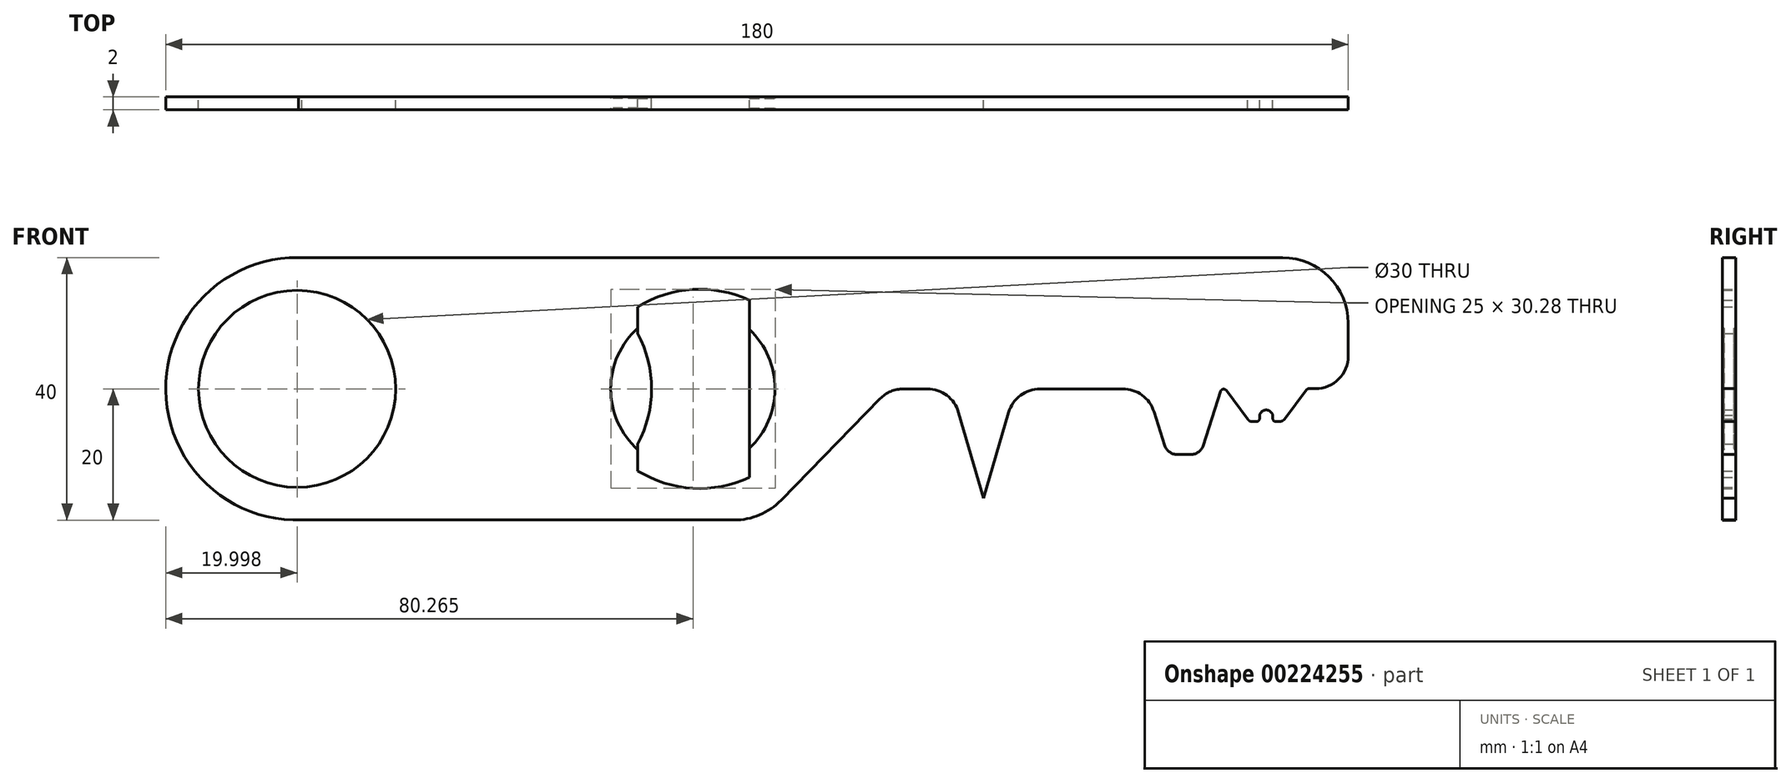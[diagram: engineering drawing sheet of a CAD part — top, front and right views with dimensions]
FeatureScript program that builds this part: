
annotation { "Feature Type Name" : "Feature", "Feature Type Description" : "" }
export const myFeature = defineFeature(function(context is Context, id is Id, definition is map)
    precondition{}
    {
        {
            var Q0;
            Q0=qCreatedBy(makeId("Front.planeOp"),FACE);
            var sketch = newSketch(context, id + "F0", { "sketchPlane" : qUnion([Q0])});
            skArc(sketch, "E0", {"start": v(-75.03, 20) * mm, "mid": v(-95.23, -0.26) * mm, "end": v(-74.5, -19.99) * mm});
            skLineSegment(sketch, "E1", {"start": v(-75.03, 20) * mm, "end": v(74.77, 20) * mm});
            skLineSegment(sketch, "E2", {"start": v(84.77, 10) * mm, "end": v(84.77, 5.03) * mm});
            skLineSegment(sketch, "E3", {"start": v(-74.5, -19.99) * mm, "end": v(-8.73, -19.99) * mm});
            skLineSegment(sketch, "E4", {"start": v(-1.56, -16.97) * mm, "end": v(13.5, -1.5) * mm});
            skCircle(sketch, "E5", {"center": v(-75.23, 0) * mm, "radius": 15 * mm});
            skPoint(sketch, "E6.start.orphan", {"position": v(-95.23, 0) * mm});
            skLineSegment(sketch, "E7", {"start": v(79.77, 0.03) * mm, "end": v(78.79, 0.03) * mm});
            skLineSegment(sketch, "E8", {"start": v(74.27, -5) * mm, "end": v(73.77, -5) * mm});
            skLineSegment(sketch, "E9", {"start": v(60.8, -10) * mm, "end": v(58.73, -10) * mm});
            skLineSegment(sketch, "E10.trimOffspring", {"start": v(70.77, -5) * mm, "end": v(70.1, -5) * mm});
            skArc(sketch, "E11", {"start": v(73.27, -4) * mm, "mid": v(72.27, -3.22) * mm, "end": v(71.27, -4) * mm});
            skLineSegment(sketch, "E12", {"start": v(73.27, -4.5) * mm, "end": v(73.27, -4) * mm});
            skLineSegment(sketch, "E13", {"start": v(71.27, -4.5) * mm, "end": v(71.27, -4) * mm});
            skArc(sketch, "E14.filletArc", {"start": v(73.27, -4.5) * mm, "mid": v(73.41, -4.85) * mm, "end": v(73.77, -5) * mm});
            skArc(sketch, "E15.filletArc", {"start": v(70.77, -5) * mm, "mid": v(71.12, -4.85) * mm, "end": v(71.27, -4.5) * mm});
            skLineSegment(sketch, "E16", {"start": v(75.07, -4.6) * mm, "end": v(78.39, -0.17) * mm});
            skArc(sketch, "E17.filletArc", {"start": v(74.27, -5) * mm, "mid": v(74.71, -4.9) * mm, "end": v(75.07, -4.6) * mm});
            skLineSegment(sketch, "E18", {"start": v(72.27, -20) * mm, "end": v(29.27, -20) * mm});
            skLineSegment(sketch, "E19", {"start": v(62.71, -8.6) * mm, "end": v(65.32, -0.39) * mm});
            skLineSegment(sketch, "E20.MirrorCS", {"start": v(69.47, -4.6) * mm, "end": v(66.2, -0.24) * mm});
            skArc(sketch, "E21", {"start": v(69.47, -4.6) * mm, "mid": v(69.73, -4.9) * mm, "end": v(70.1, -5) * mm});
            skPoint(sketch, "E22.endSnap0", {"position": v(59.77, -10) * mm});
            skLineSegment(sketch, "E23.MirrorCS", {"start": v(56.82, -8.6) * mm, "end": v(55.2, -3.49) * mm});
            skPoint(sketch, "E24.newPointA", {"position": v(65.45, 0) * mm});
            skArc(sketch, "E24.filletArc", {"start": v(66.2, -0.24) * mm, "mid": v(65.72, -0.05) * mm, "end": v(65.32, -0.39) * mm});
            skPoint(sketch, "E25.visualSharp", {"position": v(57.27, -10) * mm});
            skArc(sketch, "E25.filletArc", {"start": v(56.82, -8.6) * mm, "mid": v(57.55, -9.61) * mm, "end": v(58.73, -10) * mm});
            skPoint(sketch, "E26.visualSharp", {"position": v(62.27, -10) * mm});
            skArc(sketch, "E26.filletArc", {"start": v(60.8, -10) * mm, "mid": v(61.99, -9.61) * mm, "end": v(62.71, -8.6) * mm});
            skLineSegment(sketch, "E27", {"start": v(25.46, -3.6) * mm, "end": v(29.25, -16.67) * mm});
            skLineSegment(sketch, "E28", {"start": v(33.07, -3.6) * mm, "end": v(29.25, -16.67) * mm});
            skLineSegment(sketch, "E29", {"start": v(17.08, 0) * mm, "end": v(20.66, 0) * mm});
            skLineSegment(sketch, "E30", {"start": v(37.87, 0) * mm, "end": v(50.43, 0) * mm});
            skPoint(sketch, "E31.visualSharp", {"position": v(24.42, 0) * mm});
            skArc(sketch, "E31.filletArc", {"start": v(25.46, -3.6) * mm, "mid": v(23.66, -1) * mm, "end": v(20.66, 0) * mm});
            skPoint(sketch, "E32.visualSharp", {"position": v(14.97, 0) * mm});
            skArc(sketch, "E32.filletArc", {"start": v(17.08, 0) * mm, "mid": v(15.14, -0.4) * mm, "end": v(13.5, -1.5) * mm});
            skPoint(sketch, "E33.visualSharp", {"position": v(34.12, 0) * mm});
            skArc(sketch, "E33.filletArc", {"start": v(37.87, 0) * mm, "mid": v(34.87, -1) * mm, "end": v(33.07, -3.6) * mm});
            skPoint(sketch, "E34.visualSharp", {"position": v(54.1, 0) * mm});
            skArc(sketch, "E34.filletArc", {"start": v(55.2, -3.49) * mm, "mid": v(53.38, -0.96) * mm, "end": v(50.43, 0) * mm});
            skLineSegment(sketch, "E35", {"start": v(72.27, -16.33) * mm, "end": v(62.27, -16.33) * mm});
            skPoint(sketch, "E36.visualSharp", {"position": v(84.77, 20) * mm});
            skArc(sketch, "E36.filletArc", {"start": v(84.77, 10) * mm, "mid": v(81.84, 17.07) * mm, "end": v(74.77, 20) * mm});
            skPoint(sketch, "E37.visualSharp", {"position": v(84.77, 0.03) * mm});
            skArc(sketch, "E37.filletArc", {"start": v(79.77, 0.03) * mm, "mid": v(83.3, 1.5) * mm, "end": v(84.77, 5.03) * mm});
            skPoint(sketch, "E38.visualSharp", {"position": v(78.54, 0.03) * mm});
            skArc(sketch, "E38.filletArc", {"start": v(78.79, 0.03) * mm, "mid": v(78.56, -0.03) * mm, "end": v(78.39, -0.17) * mm});
            skPoint(sketch, "E39.visualSharp", {"position": v(-4.5, -19.99) * mm});
            skArc(sketch, "E39.filletArc", {"start": v(-8.73, -19.99) * mm, "mid": v(-4.84, -19.2) * mm, "end": v(-1.56, -16.97) * mm});
            skSolve(sketch);
        }
        {
            var Q0;
            Q0=makeQuery(id+"F0.imprint","IMPRINT",FACE,{"disambiguationData":[TD([[makeQuery(id+"F0.imprint","IMPRINT",EDGE,{"derivedFrom":sQuery(id+"F0.wireOp",EDGE,"E0")}),1.0]])]});
            extrude(context, id + "F1", {"entities" : qUnion([Q0]), "depth" : 2 * mm});
        }
        {
            var Q0;
            Q0=qCreatedBy(makeId("Front.planeOp"),FACE);
            var sketch = newSketch(context, id + "F2", { "sketchPlane" : qUnion([Q0])});
            skLineSegment(sketch, "E40", {"start": v(-6.37, 0) * mm, "end": v(-6.37, -13.5) * mm});
            skLineSegment(sketch, "E41", {"start": v(-6.37, 0) * mm, "end": v(-6.37, 13.5) * mm});
            skLineSegment(sketch, "E42", {"start": v(-23.37, 8.41) * mm, "end": v(-23.37, 12.5) * mm});
            skLineSegment(sketch, "E43", {"start": v(-23.37, -8.41) * mm, "end": v(-23.37, -12.5) * mm});
            skArc(sketch, "E44", {"start": v(-6.37, 13.5) * mm, "mid": v(-15, 15.14) * mm, "end": v(-23.37, 12.5) * mm});
            skArc(sketch, "E45", {"start": v(-23.37, -12.5) * mm, "mid": v(-15, -15.14) * mm, "end": v(-6.37, -13.5) * mm});
            skArc(sketch, "E46", {"start": v(-23.37, -8.41) * mm, "mid": v(-21.28, 0) * mm, "end": v(-23.37, 8.41) * mm});
            skPoint(sketch, "E47.orphan", {"position": v(-23.37, 0) * mm});
            skSolve(sketch);
        }
        {
            var Q0;
            Q0=makeQuery(id+"F2.imprint","IMPRINT",FACE,{"disambiguationData":[TD([[makeQuery(id+"F2.imprint","IMPRINT",EDGE,{"derivedFrom":sQuery(id+"F2.wireOp",EDGE,"E40")}),-1.0]])]});
            extrude(context, id + "F3", {"entities" : qUnion([Q0]), "operationType" : NewBodyOperationType.REMOVE, "endBound" : BoundingType.THROUGH_ALL, "depth" : 25 * mm});
        }
        {
            var Q0;
            Q0=makeQuery(id+"F1.opExtrude","CAP_FACE",FACE,{"disambiguationData":[OSD([sQuery(id+"F0.wireOp",EDGE,"E0"),sQuery(id+"F0.wireOp",EDGE,"E1"),sQuery(id+"F0.wireOp",EDGE,"E2"),sQuery(id+"F0.wireOp",EDGE,"E3"),sQuery(id+"F0.wireOp",EDGE,"E4"),sQuery(id+"F0.wireOp",EDGE,"E5"),sQuery(id+"F0.wireOp",EDGE,"E7"),sQuery(id+"F0.wireOp",EDGE,"E8"),sQuery(id+"F0.wireOp",EDGE,"E9"),sQuery(id+"F0.wireOp",EDGE,"E10.trimOffspring"),sQuery(id+"F0.wireOp",EDGE,"E11"),sQuery(id+"F0.wireOp",EDGE,"E12"),sQuery(id+"F0.wireOp",EDGE,"E13"),sQuery(id+"F0.wireOp",EDGE,"E14.filletArc"),sQuery(id+"F0.wireOp",EDGE,"E15.filletArc"),sQuery(id+"F0.wireOp",EDGE,"E16"),sQuery(id+"F0.wireOp",EDGE,"E17.filletArc"),sQuery(id+"F0.wireOp",EDGE,"E19"),sQuery(id+"F0.wireOp",EDGE,"E20.MirrorCS"),sQuery(id+"F0.wireOp",EDGE,"E21"),sQuery(id+"F0.wireOp",EDGE,"E23.MirrorCS"),sQuery(id+"F0.wireOp",EDGE,"E24.filletArc"),sQuery(id+"F0.wireOp",EDGE,"E25.filletArc"),sQuery(id+"F0.wireOp",EDGE,"E26.filletArc"),sQuery(id+"F0.wireOp",EDGE,"E27"),sQuery(id+"F0.wireOp",EDGE,"E28"),sQuery(id+"F0.wireOp",EDGE,"E29"),sQuery(id+"F0.wireOp",EDGE,"E30"),sQuery(id+"F0.wireOp",EDGE,"E31.filletArc"),sQuery(id+"F0.wireOp",EDGE,"E32.filletArc"),sQuery(id+"F0.wireOp",EDGE,"E33.filletArc"),sQuery(id+"F0.wireOp",EDGE,"E34.filletArc"),sQuery(id+"F0.wireOp",EDGE,"E36.filletArc"),sQuery(id+"F0.wireOp",EDGE,"E37.filletArc"),sQuery(id+"F0.wireOp",EDGE,"E38.filletArc"),sQuery(id+"F0.wireOp",EDGE,"E39.filletArc")])],"isStart":false});
            var sketch = newSketch(context, id + "F4", { "sketchPlane" : qUnion([Q0])});
            skCircle(sketch, "E48", {"center": v(-15, 0) * mm, "radius": 12.5 * mm});
            skPoint(sketch, "E48.centerSnap0", {"position": v(-15, 15.14) * mm});
            skSolve(sketch);
        }
        {
            var Q0;
            {var subQ0=sQuery(id+"F4.wireOp",EDGE,"E48");var subQ1=makeQuery(id+"F3.boolean.opBoolean","INTERSECT",EDGE,{"derivedFrom":[makeQuery(id+"F1.opExtrude","CAP_FACE",FACE,{"disambiguationData":[OSD([sQuery(id+"F0.wireOp",EDGE,"E0"),sQuery(id+"F0.wireOp",EDGE,"E1"),sQuery(id+"F0.wireOp",EDGE,"E2"),sQuery(id+"F0.wireOp",EDGE,"E3"),sQuery(id+"F0.wireOp",EDGE,"E4"),sQuery(id+"F0.wireOp",EDGE,"E5"),sQuery(id+"F0.wireOp",EDGE,"E7"),sQuery(id+"F0.wireOp",EDGE,"E8"),sQuery(id+"F0.wireOp",EDGE,"E9"),sQuery(id+"F0.wireOp",EDGE,"E10.trimOffspring"),sQuery(id+"F0.wireOp",EDGE,"E11"),sQuery(id+"F0.wireOp",EDGE,"E12"),sQuery(id+"F0.wireOp",EDGE,"E13"),sQuery(id+"F0.wireOp",EDGE,"E14.filletArc"),sQuery(id+"F0.wireOp",EDGE,"E15.filletArc"),sQuery(id+"F0.wireOp",EDGE,"E16"),sQuery(id+"F0.wireOp",EDGE,"E17.filletArc"),sQuery(id+"F0.wireOp",EDGE,"E19"),sQuery(id+"F0.wireOp",EDGE,"E20.MirrorCS"),sQuery(id+"F0.wireOp",EDGE,"E21"),sQuery(id+"F0.wireOp",EDGE,"E23.MirrorCS"),sQuery(id+"F0.wireOp",EDGE,"E24.filletArc"),sQuery(id+"F0.wireOp",EDGE,"E25.filletArc"),sQuery(id+"F0.wireOp",EDGE,"E26.filletArc"),sQuery(id+"F0.wireOp",EDGE,"E27"),sQuery(id+"F0.wireOp",EDGE,"E28"),sQuery(id+"F0.wireOp",EDGE,"E29"),sQuery(id+"F0.wireOp",EDGE,"E30"),sQuery(id+"F0.wireOp",EDGE,"E31.filletArc"),sQuery(id+"F0.wireOp",EDGE,"E32.filletArc"),sQuery(id+"F0.wireOp",EDGE,"E33.filletArc"),sQuery(id+"F0.wireOp",EDGE,"E34.filletArc"),sQuery(id+"F0.wireOp",EDGE,"E36.filletArc"),sQuery(id+"F0.wireOp",EDGE,"E37.filletArc"),sQuery(id+"F0.wireOp",EDGE,"E38.filletArc"),sQuery(id+"F0.wireOp",EDGE,"E39.filletArc")])],"isStart":false}),makeQuery(id+"F3.opExtrude","SWEPT_FACE",FACE,{"disambiguationData":[OSD([sQuery(id+"F2.wireOp",EDGE,"E42"),sQuery(id+"F2.wireOp",EDGE,"E43")])]})]});var subQ2=makeQuery(id+"F4.imprint","INTERSECT",VERTEX,{"disambiguationData":[OD(0.0)],"derivedFrom":[subQ1,subQ0]});Q0=makeQuery(id+"F4.imprint","IMPRINT",FACE,{"disambiguationData":[TD([[makeQuery(id+"F4.imprint","IMPRINT",EDGE,{"disambiguationData":[TD([[subQ2,-1.0]])],"derivedFrom":subQ0}),1.0]])]});}
            var Q1;
            {var subQ0=sQuery(id+"F4.wireOp",EDGE,"E48");var subQ1=makeQuery(id+"F3.boolean.opBoolean","INTERSECT",EDGE,{"derivedFrom":[makeQuery(id+"F1.opExtrude","CAP_FACE",FACE,{"disambiguationData":[OSD([sQuery(id+"F0.wireOp",EDGE,"E0"),sQuery(id+"F0.wireOp",EDGE,"E1"),sQuery(id+"F0.wireOp",EDGE,"E2"),sQuery(id+"F0.wireOp",EDGE,"E3"),sQuery(id+"F0.wireOp",EDGE,"E4"),sQuery(id+"F0.wireOp",EDGE,"E5"),sQuery(id+"F0.wireOp",EDGE,"E7"),sQuery(id+"F0.wireOp",EDGE,"E8"),sQuery(id+"F0.wireOp",EDGE,"E9"),sQuery(id+"F0.wireOp",EDGE,"E10.trimOffspring"),sQuery(id+"F0.wireOp",EDGE,"E11"),sQuery(id+"F0.wireOp",EDGE,"E12"),sQuery(id+"F0.wireOp",EDGE,"E13"),sQuery(id+"F0.wireOp",EDGE,"E14.filletArc"),sQuery(id+"F0.wireOp",EDGE,"E15.filletArc"),sQuery(id+"F0.wireOp",EDGE,"E16"),sQuery(id+"F0.wireOp",EDGE,"E17.filletArc"),sQuery(id+"F0.wireOp",EDGE,"E19"),sQuery(id+"F0.wireOp",EDGE,"E20.MirrorCS"),sQuery(id+"F0.wireOp",EDGE,"E21"),sQuery(id+"F0.wireOp",EDGE,"E23.MirrorCS"),sQuery(id+"F0.wireOp",EDGE,"E24.filletArc"),sQuery(id+"F0.wireOp",EDGE,"E25.filletArc"),sQuery(id+"F0.wireOp",EDGE,"E26.filletArc"),sQuery(id+"F0.wireOp",EDGE,"E27"),sQuery(id+"F0.wireOp",EDGE,"E28"),sQuery(id+"F0.wireOp",EDGE,"E29"),sQuery(id+"F0.wireOp",EDGE,"E30"),sQuery(id+"F0.wireOp",EDGE,"E31.filletArc"),sQuery(id+"F0.wireOp",EDGE,"E32.filletArc"),sQuery(id+"F0.wireOp",EDGE,"E33.filletArc"),sQuery(id+"F0.wireOp",EDGE,"E34.filletArc"),sQuery(id+"F0.wireOp",EDGE,"E36.filletArc"),sQuery(id+"F0.wireOp",EDGE,"E37.filletArc"),sQuery(id+"F0.wireOp",EDGE,"E38.filletArc"),sQuery(id+"F0.wireOp",EDGE,"E39.filletArc")])],"isStart":false}),makeQuery(id+"F3.opExtrude","SWEPT_FACE",FACE,{"disambiguationData":[OSD([sQuery(id+"F2.wireOp",EDGE,"E40"),sQuery(id+"F2.wireOp",EDGE,"E41")])]})]});var subQ2=makeQuery(id+"F4.imprint","INTERSECT",VERTEX,{"disambiguationData":[OD(0.0)],"derivedFrom":[subQ1,subQ0]});Q1=makeQuery(id+"F4.imprint","IMPRINT",FACE,{"disambiguationData":[TD([[makeQuery(id+"F4.imprint","IMPRINT",EDGE,{"disambiguationData":[TD([[subQ2,1.0]])],"derivedFrom":subQ0}),1.0]])]});}
            extrude(context, id + "F5", {"entities" : qUnion([Q0, Q1]), "operationType" : NewBodyOperationType.REMOVE, "oppositeDirection" : true, "depth" : 0.25 * mm});
        }
        {
            var Q0;
            Q0=qCreatedBy(makeId("Front.planeOp"),FACE);
            var sketch = newSketch(context, id + "F6", { "sketchPlane" : qUnion([Q0])});
            skCircle(sketch, "E49", {"center": v(-14.96, 0) * mm, "radius": 12.5 * mm});
            skSolve(sketch);
        }
        {
            var Q0;
            Q0=makeQuery(id+"F6.imprint","IMPRINT",FACE,{"disambiguationData":[TD([[makeQuery(id+"F6.imprint","IMPRINT",EDGE,{"derivedFrom":sQuery(id+"F6.wireOp",EDGE,"E49")}),1.0]])]});
            extrude(context, id + "F7", {"entities" : qUnion([Q0]), "operationType" : NewBodyOperationType.REMOVE, "depth" : 0.25 * mm});
        }
    });
